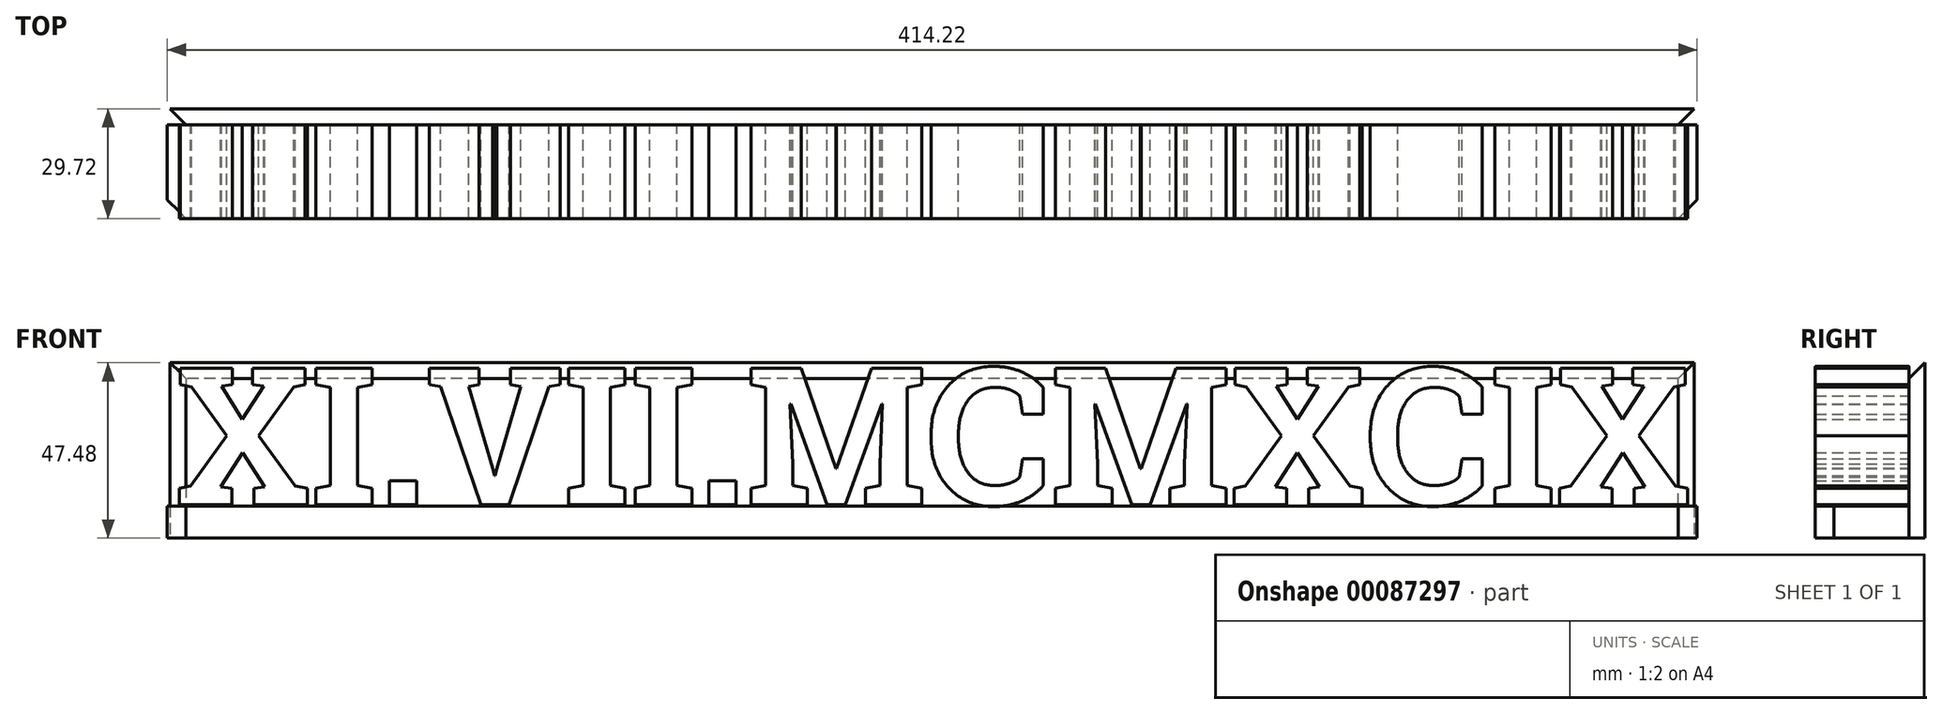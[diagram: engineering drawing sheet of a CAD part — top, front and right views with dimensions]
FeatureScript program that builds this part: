
annotation { "Feature Type Name" : "Feature", "Feature Type Description" : "" }
export const myFeature = defineFeature(function(context is Context, id is Id, definition is map)
    precondition{}
    {
        {
            var Q0;
            Q0=qCreatedBy(makeId("Front.planeOp"),FACE);
            var sketch = newSketch(context, id + "F0", { "sketchPlane" : qUnion([Q0])});
            skText(sketch, "E0", { "text": "XI.VII.MCMXCIX", "fontName": "RobotoSlab-Bold.ttf"});
            const initialGuessF0  = {"E0": [-0.2066, -0.01629, 1, 0, 0.03736]};
            skSetInitialGuess(sketch, initialGuessF0);
            skSolve(sketch);
        }
        {
            var Q0;
            Q0=makeQuery(id+"F0.imprint","IMPRINT",FACE,{"disambiguationData":[TD([[makeQuery(id+"F0.imprint","IMPRINT",EDGE,{"derivedFrom":sQuery(id+"F0.wireOp",EDGE,"E0.sketch_text.stroke-0")}),-1.0]])]});
            var Q1;
            Q1=makeQuery(id+"F0.imprint","IMPRINT",FACE,{"disambiguationData":[TD([[makeQuery(id+"F0.imprint","IMPRINT",EDGE,{"derivedFrom":sQuery(id+"F0.wireOp",EDGE,"E0.sketch_text.stroke-28")}),-1.0]])]});
            var Q2;
            Q2=makeQuery(id+"F0.imprint","IMPRINT",FACE,{"disambiguationData":[TD([[makeQuery(id+"F0.imprint","IMPRINT",EDGE,{"derivedFrom":sQuery(id+"F0.wireOp",EDGE,"E0.sketch_text.stroke-40")}),-1.0]])]});
            var Q3;
            Q3=makeQuery(id+"F0.imprint","IMPRINT",FACE,{"disambiguationData":[TD([[makeQuery(id+"F0.imprint","IMPRINT",EDGE,{"derivedFrom":sQuery(id+"F0.wireOp",EDGE,"E0.sketch_text.stroke-44")}),-1.0]])]});
            var Q4;
            Q4=makeQuery(id+"F0.imprint","IMPRINT",FACE,{"disambiguationData":[TD([[makeQuery(id+"F0.imprint","IMPRINT",EDGE,{"derivedFrom":sQuery(id+"F0.wireOp",EDGE,"E0.sketch_text.stroke-62")}),-1.0]])]});
            var Q5;
            Q5=makeQuery(id+"F0.imprint","IMPRINT",FACE,{"disambiguationData":[TD([[makeQuery(id+"F0.imprint","IMPRINT",EDGE,{"derivedFrom":sQuery(id+"F0.wireOp",EDGE,"E0.sketch_text.stroke-74")}),-1.0]])]});
            var Q6;
            Q6=makeQuery(id+"F0.imprint","IMPRINT",FACE,{"disambiguationData":[TD([[makeQuery(id+"F0.imprint","IMPRINT",EDGE,{"derivedFrom":sQuery(id+"F0.wireOp",EDGE,"E0.sketch_text.stroke-86")}),-1.0]])]});
            var Q7;
            Q7=makeQuery(id+"F0.imprint","IMPRINT",FACE,{"disambiguationData":[TD([[makeQuery(id+"F0.imprint","IMPRINT",EDGE,{"derivedFrom":sQuery(id+"F0.wireOp",EDGE,"E0.sketch_text.stroke-90")}),-1.0]])]});
            var Q8;
            Q8=makeQuery(id+"F0.imprint","IMPRINT",FACE,{"disambiguationData":[TD([[makeQuery(id+"F0.imprint","IMPRINT",EDGE,{"derivedFrom":sQuery(id+"F0.wireOp",EDGE,"E0.sketch_text.stroke-121")}),-1.0]])]});
            var Q9;
            Q9=makeQuery(id+"F0.imprint","IMPRINT",FACE,{"disambiguationData":[TD([[makeQuery(id+"F0.imprint","IMPRINT",EDGE,{"derivedFrom":sQuery(id+"F0.wireOp",EDGE,"E0.sketch_text.stroke-145")}),-1.0]])]});
            var Q10;
            Q10=makeQuery(id+"F0.imprint","IMPRINT",FACE,{"disambiguationData":[TD([[makeQuery(id+"F0.imprint","IMPRINT",EDGE,{"derivedFrom":sQuery(id+"F0.wireOp",EDGE,"E0.sketch_text.stroke-176")}),-1.0]])]});
            var Q11;
            Q11=makeQuery(id+"F0.imprint","IMPRINT",FACE,{"disambiguationData":[TD([[makeQuery(id+"F0.imprint","IMPRINT",EDGE,{"derivedFrom":sQuery(id+"F0.wireOp",EDGE,"E0.sketch_text.stroke-204")}),-1.0]])]});
            var Q12;
            Q12=makeQuery(id+"F0.imprint","IMPRINT",FACE,{"disambiguationData":[TD([[makeQuery(id+"F0.imprint","IMPRINT",EDGE,{"derivedFrom":sQuery(id+"F0.wireOp",EDGE,"E0.sketch_text.stroke-228")}),-1.0]])]});
            var Q13;
            Q13=makeQuery(id+"F0.imprint","IMPRINT",FACE,{"disambiguationData":[TD([[makeQuery(id+"F0.imprint","IMPRINT",EDGE,{"derivedFrom":sQuery(id+"F0.wireOp",EDGE,"E0.sketch_text.stroke-240")}),-1.0]])]});
            extrude(context, id + "F1", {"entities" : qUnion([Q0, Q1, Q2, Q3, Q4, Q5, Q6, Q7, Q8, Q9, Q10, Q11, Q12, Q13]), "depth" : 25.4 * mm});
        }
        {
            var Q0;
            Q0=qCreatedBy(makeId("Front.planeOp"),FACE);
            var sketch = newSketch(context, id + "F2", { "sketchPlane" : qUnion([Q0])});
            skLineSegment(sketch, "E1.bottom", {"start": v(205.27, 22.9) * mm, "end": v(-208.95, 22.9) * mm});
            skLineSegment(sketch, "E1.top", {"start": v(205.27, -25.35) * mm, "end": v(-208.95, -25.35) * mm});
            skLineSegment(sketch, "E1.left", {"start": v(205.27, 22.9) * mm, "end": v(205.27, -25.35) * mm});
            skLineSegment(sketch, "E1.right", {"start": v(-208.95, 22.9) * mm, "end": v(-208.95, -25.35) * mm});
            skSolve(sketch);
        }
        {
            var Q0;
            Q0=makeQuery(id+"F2.imprint","IMPRINT",FACE,{"disambiguationData":[TD([[makeQuery(id+"F2.imprint","IMPRINT",EDGE,{"derivedFrom":sQuery(id+"F2.wireOp",EDGE,"E1.bottom")}),1.0]])]});
            extrude(context, id + "F3", {"entities" : qUnion([Q0]), "oppositeDirection" : true, "depth" : 4.32 * mm});
        }
        {
            var Q0;
            Q0=makeQuery(id+"F3.opExtrude","CAP_FACE",FACE,{"disambiguationData":[OSD([sQuery(id+"F2.wireOp",EDGE,"E1.bottom"),sQuery(id+"F2.wireOp",EDGE,"E1.top"),sQuery(id+"F2.wireOp",EDGE,"E1.left"),sQuery(id+"F2.wireOp",EDGE,"E1.right")])],"isStart":true});
            var sketch = newSketch(context, id + "F4", { "sketchPlane" : qUnion([Q0])});
            skLineSegment(sketch, "E2.bottom", {"start": v(-208.95, -16.75) * mm, "end": v(205.27, -16.75) * mm});
            skLineSegment(sketch, "E2.top", {"start": v(-208.95, -25.35) * mm, "end": v(205.27, -25.35) * mm});
            skLineSegment(sketch, "E2.left", {"start": v(-208.95, -16.75) * mm, "end": v(-208.95, -25.35) * mm});
            skLineSegment(sketch, "E2.right", {"start": v(205.27, -16.75) * mm, "end": v(205.27, -25.35) * mm});
            skSolve(sketch);
        }
        {
            var Q0;
            Q0 = qSketchRegion(id + "F4", true);
            extrude(context, id + "F5", {"entities" : qUnion([Q0]), "depth" : 25.4 * mm});
        }
        {
            var Q0;
            Q0=makeQuery(id+"F3.opExtrude","CAP_EDGE",EDGE,{"disambiguationData":[OSD([sQuery(id+"F2.wireOp",EDGE,"E1.bottom")])],"isStart":true});
            var Q1;
            Q1=makeQuery(id+"F3.opExtrude","CAP_EDGE",EDGE,{"disambiguationData":[OSD([sQuery(id+"F2.wireOp",EDGE,"E1.right")])],"isStart":true});
            var Q2;
            Q2=makeQuery(id+"F3.opExtrude","CAP_EDGE",EDGE,{"disambiguationData":[OSD([sQuery(id+"F2.wireOp",EDGE,"E1.left")])],"isStart":true});
            chamfer(context, id + "F6", {"entities" : qUnion([Q0, Q1, Q2]), "width" : 5.08 * mm, "tangentPropagation" : true});
        }
        {
            var Q0;
            Q0=makeQuery(id+"F5.opExtrude","CAP_EDGE",EDGE,{"disambiguationData":[OSD([sQuery(id+"F4.wireOp",EDGE,"E2.right")])],"isStart":false});
            var Q1;
            Q1=makeQuery(id+"F5.opExtrude","CAP_EDGE",EDGE,{"disambiguationData":[OSD([sQuery(id+"F4.wireOp",EDGE,"E2.left")])],"isStart":false});
            chamfer(context, id + "F7", {"entities" : qUnion([Q0, Q1]), "width" : 5.08 * mm, "tangentPropagation" : true});
        }
    });
